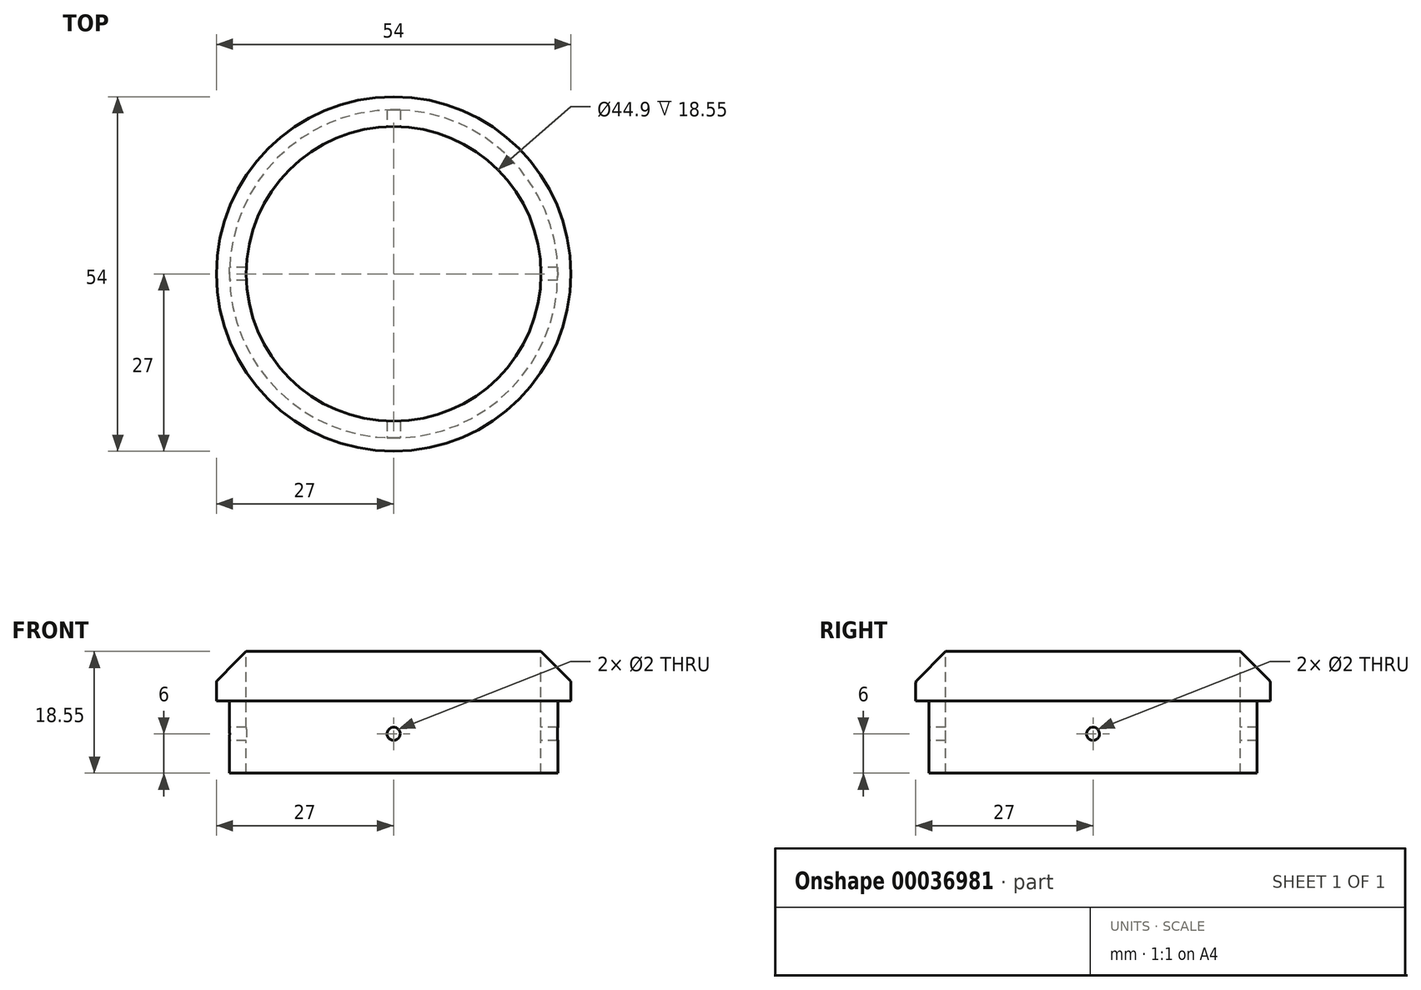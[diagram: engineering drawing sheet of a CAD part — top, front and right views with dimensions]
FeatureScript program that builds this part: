
annotation { "Feature Type Name" : "Feature", "Feature Type Description" : "" }
export const myFeature = defineFeature(function(context is Context, id is Id, definition is map)
    precondition{}
    {
        {
            var Q0;
            Q0=qCreatedBy(makeId("Top.planeOp"),FACE);
            var sketch = newSketch(context, id + "F0", { "sketchPlane" : qUnion([Q0])});
            skCircle(sketch, "E0", {"center": v(0, 0) * mm, "radius": 27 * mm});
            skSolve(sketch);
        }
        {
            var Q0;
            Q0 = qSketchRegion(id + "F0", true);
            extrude(context, id + "F1", {"entities" : qUnion([Q0]), "depth" : 8 * mm});
        }
        {
            var Q0;
            Q0=makeQuery(id+"F1.opExtrude","CAP_EDGE",EDGE,{"disambiguationData":[OSD([sQuery(id+"F0.wireOp",EDGE,"E0")])],"isStart":false});
            chamfer(context, id + "F2", {"entities" : qUnion([Q0]), "width" : 5 * mm, "tangentPropagation" : true});
        }
        {
            var Q0;
            {var subQ0=sQuery(id+"F0.wireOp",EDGE,"E0");Q0=makeQuery(id+"F2.opChamfer","BLEND_EDGE",EDGE,{"blendedFrom":[makeQuery(id+"F1.opExtrude","CAP_EDGE",EDGE,{"disambiguationData":[OSD([subQ0])],"isStart":false}),makeQuery(id+"F1.opExtrude","CAP_FACE",FACE,{"disambiguationData":[OSD([subQ0])],"isStart":false})],"blendedInto":[makeQuery(id+"F1.opExtrude","CAP_FACE",FACE,{"disambiguationData":[OSD([subQ0])],"isStart":false})]});}
            var Q1;
            {var subQ0=sQuery(id+"F0.wireOp",EDGE,"E0");Q1=makeQuery(id+"F2.opChamfer","BLEND_EDGE",EDGE,{"blendedFrom":[makeQuery(id+"F1.opExtrude","CAP_EDGE",EDGE,{"disambiguationData":[OSD([subQ0])],"isStart":false}),makeQuery(id+"F1.opExtrude","SWEPT_FACE",FACE,{"disambiguationData":[OSD([subQ0])]})],"blendedInto":[makeQuery(id+"F1.opExtrude","SWEPT_FACE",FACE,{"disambiguationData":[OSD([subQ0])]})]});}
            fillet(context, id + "F3", {"entities" : qUnion([Q0, Q1]), "radius" : 0.5 * mm, "tangentPropagation" : true, "allowEdgeOverflow" : false});
        }
        {
            var Q0;
            Q0=makeQuery(id+"F1.opExtrude","CAP_FACE",FACE,{"disambiguationData":[OSD([sQuery(id+"F0.wireOp",EDGE,"E0")])],"isStart":true});
            var sketch = newSketch(context, id + "F4", { "sketchPlane" : qUnion([Q0])});
            skCircle(sketch, "E1", {"center": v(0, 0) * mm, "radius": 25 * mm});
            skSolve(sketch);
        }
        {
            var Q0;
            Q0 = qSketchRegion(id + "F4", true);
            extrude(context, id + "F5", {"entities" : qUnion([Q0]), "operationType" : NewBodyOperationType.ADD, "depth" : 11 * mm});
        }
        {
            var Q0;
            Q0=makeQuery(id+"F1.opExtrude","CAP_FACE",FACE,{"disambiguationData":[OSD([sQuery(id+"F0.wireOp",EDGE,"E0")])],"isStart":false});
            var sketch = newSketch(context, id + "F6", { "sketchPlane" : qUnion([Q0])});
            skCircle(sketch, "E2", {"center": v(0, 0) * mm, "radius": 22.45 * mm});
            skSolve(sketch);
        }
        {
            var Q0;
            Q0 = qSketchRegion(id + "F6", true);
            extrude(context, id + "F7", {"entities" : qUnion([Q0]), "operationType" : NewBodyOperationType.REMOVE, "endBound" : BoundingType.THROUGH_ALL, "oppositeDirection" : true, "depth" : 25 * mm});
        }
        {
            var Q0;
            Q0=qCreatedBy(makeId("Front.planeOp"),FACE);
            var sketch = newSketch(context, id + "F8", { "sketchPlane" : qUnion([Q0])});
            skCircle(sketch, "E3", {"center": v(0, -5) * mm, "radius": 1 * mm});
            skSolve(sketch);
        }
        {
            var Q0;
            Q0 = qSketchRegion(id + "F8", true);
            extrude(context, id + "F9", {"entities" : qUnion([Q0]), "operationType" : NewBodyOperationType.REMOVE, "endBound" : BoundingType.THROUGH_ALL, "oppositeDirection" : true, "depth" : 25 * mm, "hasSecondDirection" : true, "secondDirectionBound" : SecondDirectionBoundingType.THROUGH_ALL, "secondDirectionOppositeDirection" : false, "secondDirectionDepth" : 25 * mm});
        }
        {
            var Q0;
            Q0=qCreatedBy(makeId("Right.planeOp"),FACE);
            var sketch = newSketch(context, id + "F10", { "sketchPlane" : qUnion([Q0])});
            skCircle(sketch, "E4", {"center": v(0, -5) * mm, "radius": 1 * mm});
            skSolve(sketch);
        }
        {
            var Q0;
            Q0 = qSketchRegion(id + "F10", true);
            extrude(context, id + "F11", {"entities" : qUnion([Q0]), "operationType" : NewBodyOperationType.REMOVE, "endBound" : BoundingType.THROUGH_ALL, "depth" : 25 * mm, "hasSecondDirection" : true, "secondDirectionBound" : SecondDirectionBoundingType.THROUGH_ALL, "secondDirectionOppositeDirection" : true, "secondDirectionDepth" : 25 * mm});
        }
    });
